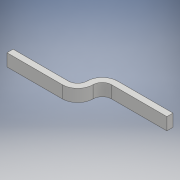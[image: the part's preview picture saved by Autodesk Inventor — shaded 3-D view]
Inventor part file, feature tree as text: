
AUTODESK INVENTOR PART (.ipt)
format: ipt  version: 2018 (Build 220112000, 112)  size: 112,128 bytes
history: native  units: mm
features: plane x1, sweep x1, sketch x1
ambient origin geometry x8: Origin, YZ Plane, XZ Plane, XY Plane, X Axis, Y Axis, Z Axis, Center Point
bodies: Body1 (feature_tree)
feature tree (3):
  plane  "Work Plane1"
  sweep  "Sweep1"
  sketch  "Sketch3"  dims[d9=44.0mm d15=8.0mm d16=22.0mm d17=22.0mm d20=4.0mm d21=2.0mm d22=0.0mm d23=0.0mm d24=4.0mm]
